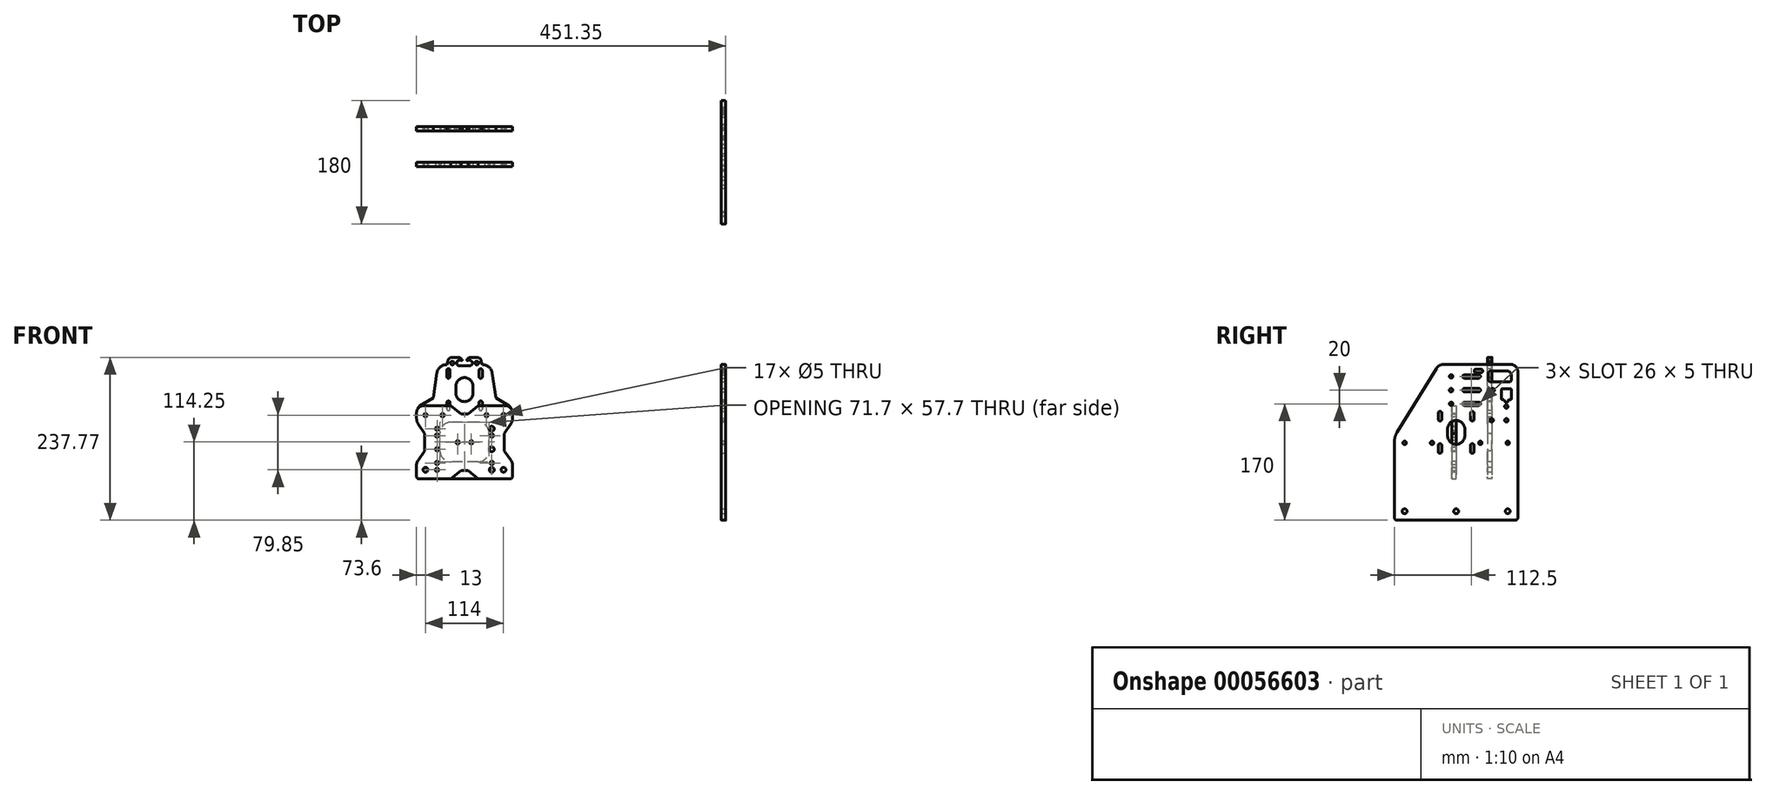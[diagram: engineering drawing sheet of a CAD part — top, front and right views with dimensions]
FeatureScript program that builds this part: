
annotation { "Feature Type Name" : "Feature", "Feature Type Description" : "" }
export const myFeature = defineFeature(function(context is Context, id is Id, definition is map)
    precondition{}
    {
        {
            var Q0;
            Q0=qCreatedBy(makeId("Right.planeOp"),FACE);
            var sketch = newSketch(context, id + "F0", { "sketchPlane" : qUnion([Q0])});
            skLineSegment(sketch, "E0", {"start": v(-28.77, 108.05) * mm, "end": v(-86.28, 14.78) * mm});
            skLineSegment(sketch, "E1", {"start": v(-90, 1.66) * mm, "end": v(-90, -110.25) * mm});
            skLineSegment(sketch, "E2", {"start": v(-86.5, -113.75) * mm, "end": v(86.5, -113.75) * mm});
            skLineSegment(sketch, "E3", {"start": v(90, -110.25) * mm, "end": v(90, 103.75) * mm});
            skLineSegment(sketch, "E4", {"start": v(80, 113.75) * mm, "end": v(-18.55, 113.75) * mm});
            skLineSegment(sketch, "E5", {"start": v(0, -113.75) * mm, "end": v(0, 0) * mm, "construction": true});
            skLineSegment(sketch, "E6", {"start": v(0, 0) * mm, "end": v(0, 113.75) * mm, "construction": true});
            skPoint(sketch, "E7.visualSharp", {"position": v(-25.25, 113.75) * mm});
            skArc(sketch, "E7.filletArc", {"start": v(-18.55, 113.75) * mm, "mid": v(-24.4, 112.23) * mm, "end": v(-28.77, 108.05) * mm});
            skPoint(sketch, "E8.visualSharp", {"position": v(90, 113.75) * mm});
            skArc(sketch, "E8.filletArc", {"start": v(90, 103.75) * mm, "mid": v(87.07, 110.82) * mm, "end": v(80, 113.75) * mm});
            skPoint(sketch, "E9.visualSharp", {"position": v(-90, -113.75) * mm});
            skArc(sketch, "E9.filletArc", {"start": v(-90, -110.25) * mm, "mid": v(-88.97, -112.72) * mm, "end": v(-86.5, -113.75) * mm});
            skPoint(sketch, "E10.visualSharp", {"position": v(90, -113.75) * mm});
            skArc(sketch, "E10.filletArc", {"start": v(86.5, -113.75) * mm, "mid": v(88.97, -112.72) * mm, "end": v(90, -110.25) * mm});
            skPoint(sketch, "E11.visualSharp", {"position": v(-90, 8.75) * mm});
            skArc(sketch, "E11.filletArc", {"start": v(-86.28, 14.78) * mm, "mid": v(-89.05, 8.48) * mm, "end": v(-90, 1.66) * mm});
            skSolve(sketch);
        }
        {
            var Q0;
            Q0 = qSketchRegion(id + "F0", true);
            extrude(context, id + "F1", {"entities" : qUnion([Q0]), "depth" : 6.35 * mm});
        }
        {
            var Q0;
            Q0=makeQuery(id+"F1.opExtrude","CAP_FACE",FACE,{"disambiguationData":[OSD([sQuery(id+"F0.wireOp",EDGE,"E0"),sQuery(id+"F0.wireOp",EDGE,"E1"),sQuery(id+"F0.wireOp",EDGE,"E2"),sQuery(id+"F0.wireOp",EDGE,"E3"),sQuery(id+"F0.wireOp",EDGE,"E4"),sQuery(id+"F0.wireOp",EDGE,"E7.filletArc"),sQuery(id+"F0.wireOp",EDGE,"E8.filletArc"),sQuery(id+"F0.wireOp",EDGE,"E9.filletArc"),sQuery(id+"F0.wireOp",EDGE,"E10.filletArc"),sQuery(id+"F0.wireOp",EDGE,"E11.filletArc")])],"isStart":false});
            var sketch = newSketch(context, id + "F2", { "sketchPlane" : qUnion([Q0])});
            skLineSegment(sketch, "E12", {"start": v(0, 0) * mm, "end": v(0, -100.75) * mm, "construction": true});
            skLineSegment(sketch, "E13", {"start": v(0, -100.75) * mm, "end": v(75.3, -100.75) * mm, "construction": true});
            skLineSegment(sketch, "E14", {"start": v(0, -100.75) * mm, "end": v(-75.3, -100.75) * mm, "construction": true});
            skCircle(sketch, "E15", {"center": v(-75.3, -100.75) * mm, "radius": 3.57 * mm});
            skCircle(sketch, "E16", {"center": v(75.3, -100.75) * mm, "radius": 3.57 * mm});
            skCircle(sketch, "E17", {"center": v(0, -100.75) * mm, "radius": 3.57 * mm});
            skLineSegment(sketch, "E18", {"start": v(-75.3, -0.75) * mm, "end": v(-35.3, -0.75) * mm, "construction": true});
            skLineSegment(sketch, "E19", {"start": v(-35.3, -0.75) * mm, "end": v(0, -0.75) * mm, "construction": true});
            skLineSegment(sketch, "E20", {"start": v(0, -0.75) * mm, "end": v(35.3, -0.75) * mm, "construction": true});
            skLineSegment(sketch, "E21", {"start": v(35.3, -0.75) * mm, "end": v(75.3, -0.75) * mm, "construction": true});
            skCircle(sketch, "E22", {"center": v(-75.3, -0.75) * mm, "radius": 2.5 * mm});
            skCircle(sketch, "E23", {"center": v(-35.3, -0.75) * mm, "radius": 2.5 * mm});
            skCircle(sketch, "E24", {"center": v(35.3, -0.75) * mm, "radius": 2.5 * mm});
            skCircle(sketch, "E25", {"center": v(75.3, -0.75) * mm, "radius": 2.5 * mm});
            skLineSegment(sketch, "E26", {"start": v(-75.3, -0.75) * mm, "end": v(-75.3, -100.75) * mm, "construction": true});
            skLineSegment(sketch, "E27", {"start": v(75.3, -0.75) * mm, "end": v(75.3, -100.75) * mm, "construction": true});
            skSolve(sketch);
        }
        {
            var Q0;
            Q0 = qSketchRegion(id + "F2", true);
            extrude(context, id + "F3", {"entities" : qUnion([Q0]), "operationType" : NewBodyOperationType.REMOVE, "endBound" : BoundingType.THROUGH_ALL, "oppositeDirection" : true, "depth" : 25 * mm});
        }
        {
            var Q0;
            Q0=makeQuery(id+"F1.opExtrude","CAP_FACE",FACE,{"disambiguationData":[OSD([sQuery(id+"F0.wireOp",EDGE,"E0"),sQuery(id+"F0.wireOp",EDGE,"E1"),sQuery(id+"F0.wireOp",EDGE,"E2"),sQuery(id+"F0.wireOp",EDGE,"E3"),sQuery(id+"F0.wireOp",EDGE,"E4"),sQuery(id+"F0.wireOp",EDGE,"E7.filletArc"),sQuery(id+"F0.wireOp",EDGE,"E8.filletArc"),sQuery(id+"F0.wireOp",EDGE,"E9.filletArc"),sQuery(id+"F0.wireOp",EDGE,"E10.filletArc"),sQuery(id+"F0.wireOp",EDGE,"E11.filletArc")])],"isStart":false});
            var sketch = newSketch(context, id + "F4", { "sketchPlane" : qUnion([Q0])});
            skArc(sketch, "E28", {"start": v(-12.5, 9.55) * mm, "mid": v(0, -2.95) * mm, "end": v(12.5, 9.55) * mm});
            skLineSegment(sketch, "E29", {"start": v(-12.5, 9.55) * mm, "end": v(-12.5, 19.55) * mm});
            skLineSegment(sketch, "E30", {"start": v(12.5, 19.55) * mm, "end": v(12.5, 9.55) * mm});
            skArc(sketch, "E31", {"start": v(-12.5, 19.55) * mm, "mid": v(0, 32.05) * mm, "end": v(12.5, 19.55) * mm});
            skLineSegment(sketch, "E32", {"start": v(0, 19.55) * mm, "end": v(0, 9.55) * mm, "construction": true});
            skLineSegment(sketch, "E33", {"start": v(-35.3, -0.75) * mm, "end": v(35.3, -0.75) * mm, "construction": true});
            skLineSegment(sketch, "E34", {"start": v(-23.57, 42.62) * mm, "end": v(-23.57, 33.62) * mm, "construction": true});
            skArc(sketch, "E35", {"start": v(-21.02, 42.62) * mm, "mid": v(-23.57, 45.17) * mm, "end": v(-26.12, 42.62) * mm});
            skArc(sketch, "E36", {"start": v(-26.12, 33.62) * mm, "mid": v(-23.57, 31.07) * mm, "end": v(-21.02, 33.62) * mm});
            skLineSegment(sketch, "E37", {"start": v(-21.02, 42.62) * mm, "end": v(-21.02, 33.62) * mm});
            skLineSegment(sketch, "E38", {"start": v(-26.12, 33.62) * mm, "end": v(-26.12, 42.62) * mm});
            skLineSegment(sketch, "E39", {"start": v(-12.5, 14.55) * mm, "end": v(12.5, 14.55) * mm, "construction": true});
            skLineSegment(sketch, "E40.MirrorCS", {"start": v(23.57, 42.62) * mm, "end": v(23.57, 33.62) * mm, "construction": true});
            skArc(sketch, "E41.MirrorCS", {"start": v(26.12, 33.62) * mm, "mid": v(23.57, 31.07) * mm, "end": v(21.02, 33.62) * mm});
            skLineSegment(sketch, "E42.MirrorCS", {"start": v(21.02, 42.62) * mm, "end": v(21.02, 33.62) * mm});
            skArc(sketch, "E43.MirrorCS", {"start": v(21.02, 42.62) * mm, "mid": v(23.57, 45.17) * mm, "end": v(26.12, 42.62) * mm});
            skLineSegment(sketch, "E44.MirrorCS", {"start": v(26.12, 33.62) * mm, "end": v(26.12, 42.62) * mm});
            skArc(sketch, "E45.MirrorCS", {"start": v(26.12, -4.52) * mm, "mid": v(23.57, -1.97) * mm, "end": v(21.02, -4.52) * mm});
            skLineSegment(sketch, "E46.MirrorCS", {"start": v(26.12, -4.52) * mm, "end": v(26.12, -13.52) * mm});
            skLineSegment(sketch, "E47.MirrorCS", {"start": v(-23.57, -13.52) * mm, "end": v(-23.57, -4.52) * mm, "construction": true});
            skLineSegment(sketch, "E48.MirrorCS", {"start": v(23.57, -13.52) * mm, "end": v(23.57, -4.52) * mm, "construction": true});
            skArc(sketch, "E49.MirrorCS", {"start": v(21.02, -13.52) * mm, "mid": v(23.57, -16.07) * mm, "end": v(26.12, -13.52) * mm});
            skLineSegment(sketch, "E50.MirrorCS", {"start": v(21.02, -13.52) * mm, "end": v(21.02, -4.52) * mm});
            skArc(sketch, "E51.MirrorCS", {"start": v(-26.12, -4.52) * mm, "mid": v(-23.57, -1.97) * mm, "end": v(-21.02, -4.52) * mm});
            skLineSegment(sketch, "E52.MirrorCS", {"start": v(-21.02, -13.52) * mm, "end": v(-21.02, -4.52) * mm});
            skArc(sketch, "E53.MirrorCS", {"start": v(-21.02, -13.52) * mm, "mid": v(-23.57, -16.07) * mm, "end": v(-26.12, -13.52) * mm});
            skLineSegment(sketch, "E54.MirrorCS", {"start": v(-26.12, -4.52) * mm, "end": v(-26.12, -13.52) * mm});
            skLineSegment(sketch, "E55", {"start": v(-23.57, 38.12) * mm, "end": v(23.57, -9.02) * mm, "construction": true});
            skLineSegment(sketch, "E56", {"start": v(23.57, -9.02) * mm, "end": v(-23.57, -9.02) * mm, "construction": true});
            skLineSegment(sketch, "E57", {"start": v(-23.57, -9.02) * mm, "end": v(23.57, 38.12) * mm, "construction": true});
            skSolve(sketch);
        }
        {
            var Q0;
            Q0 = qSketchRegion(id + "F4", true);
            extrude(context, id + "F5", {"entities" : qUnion([Q0]), "operationType" : NewBodyOperationType.REMOVE, "endBound" : BoundingType.THROUGH_ALL, "oppositeDirection" : true, "depth" : 25 * mm});
        }
        {
            var Q0;
            Q0=makeQuery(id+"F1.opExtrude","CAP_FACE",FACE,{"disambiguationData":[OSD([sQuery(id+"F0.wireOp",EDGE,"E0"),sQuery(id+"F0.wireOp",EDGE,"E1"),sQuery(id+"F0.wireOp",EDGE,"E2"),sQuery(id+"F0.wireOp",EDGE,"E3"),sQuery(id+"F0.wireOp",EDGE,"E4"),sQuery(id+"F0.wireOp",EDGE,"E7.filletArc"),sQuery(id+"F0.wireOp",EDGE,"E8.filletArc"),sQuery(id+"F0.wireOp",EDGE,"E9.filletArc"),sQuery(id+"F0.wireOp",EDGE,"E10.filletArc"),sQuery(id+"F0.wireOp",EDGE,"E11.filletArc")])],"isStart":false});
            var sketch = newSketch(context, id + "F6", { "sketchPlane" : qUnion([Q0])});
            skCircle(sketch, "E58", {"center": v(-7.35, 96.25) * mm, "radius": 2.5 * mm});
            skLineSegment(sketch, "E59", {"start": v(-7.35, 96.25) * mm, "end": v(12, 96.25) * mm, "construction": true});
            skLineSegment(sketch, "E60", {"start": v(12, 96.25) * mm, "end": v(33, 96.25) * mm, "construction": true});
            skArc(sketch, "E61", {"start": v(12, 93.75) * mm, "mid": v(9.5, 96.25) * mm, "end": v(12, 98.75) * mm});
            skArc(sketch, "E62", {"start": v(33, 98.75) * mm, "mid": v(35.5, 96.25) * mm, "end": v(33, 93.75) * mm});
            skLineSegment(sketch, "E63", {"start": v(12, 98.75) * mm, "end": v(33, 98.75) * mm});
            skLineSegment(sketch, "E64", {"start": v(12, 93.75) * mm, "end": v(33, 93.75) * mm});
            skCircle(sketch, "E65.0.1.0", {"center": v(-7.35, 76.25) * mm, "radius": 2.5 * mm});
            skLineSegment(sketch, "E65.0.1.1", {"start": v(-7.35, 76.25) * mm, "end": v(12, 76.25) * mm, "construction": true});
            skArc(sketch, "E65.0.1.2", {"start": v(12, 73.75) * mm, "mid": v(9.5, 76.25) * mm, "end": v(12, 78.75) * mm});
            skLineSegment(sketch, "E65.0.1.3", {"start": v(12, 78.75) * mm, "end": v(33, 78.75) * mm});
            skLineSegment(sketch, "E65.0.1.4", {"start": v(12, 73.75) * mm, "end": v(33, 73.75) * mm});
            skArc(sketch, "E65.0.1.5", {"start": v(33, 78.75) * mm, "mid": v(35.5, 76.25) * mm, "end": v(33, 73.75) * mm});
            skCircle(sketch, "E65.0.2.0", {"center": v(-7.35, 56.25) * mm, "radius": 2.5 * mm});
            skLineSegment(sketch, "E65.0.2.1", {"start": v(-7.35, 56.25) * mm, "end": v(12, 56.25) * mm, "construction": true});
            skArc(sketch, "E65.0.2.2", {"start": v(12, 53.75) * mm, "mid": v(9.5, 56.25) * mm, "end": v(12, 58.75) * mm});
            skLineSegment(sketch, "E65.0.2.3", {"start": v(12, 58.75) * mm, "end": v(33, 58.75) * mm});
            skLineSegment(sketch, "E65.0.2.4", {"start": v(12, 53.75) * mm, "end": v(33, 53.75) * mm});
            skArc(sketch, "E65.0.2.5", {"start": v(33, 58.75) * mm, "mid": v(35.5, 56.25) * mm, "end": v(33, 53.75) * mm});
            skLineSegment(sketch, "E65.direction1", {"start": v(-7.35, 96.25) * mm, "end": v(-7.35, 96.25) * mm});
            skLineSegment(sketch, "E65.direction2", {"start": v(-7.35, 96.25) * mm, "end": v(-7.35, 76.25) * mm, "construction": true});
            skLineSegment(sketch, "E66", {"start": v(33, 76.25) * mm, "end": v(12, 76.25) * mm, "construction": true});
            skLineSegment(sketch, "E67", {"start": v(12, 56.25) * mm, "end": v(33, 56.25) * mm, "construction": true});
            skLineSegment(sketch, "E68", {"start": v(33, 76.25) * mm, "end": v(53.35, 76.25) * mm, "construction": true});
            skPoint(sketch, "E68.endSnap0", {"position": v(35.5, 76.25) * mm});
            skCircle(sketch, "E69", {"center": v(53.35, 76.25) * mm, "radius": 2.5 * mm});
            skSolve(sketch);
        }
        {
            var Q0;
            Q0 = qSketchRegion(id + "F6", true);
            extrude(context, id + "F7", {"entities" : qUnion([Q0]), "operationType" : NewBodyOperationType.REMOVE, "endBound" : BoundingType.THROUGH_ALL, "oppositeDirection" : true, "depth" : 25 * mm});
        }
        {
            var Q0;
            Q0=makeQuery(id+"F1.opExtrude","CAP_FACE",FACE,{"disambiguationData":[OSD([sQuery(id+"F0.wireOp",EDGE,"E0"),sQuery(id+"F0.wireOp",EDGE,"E1"),sQuery(id+"F0.wireOp",EDGE,"E2"),sQuery(id+"F0.wireOp",EDGE,"E3"),sQuery(id+"F0.wireOp",EDGE,"E4"),sQuery(id+"F0.wireOp",EDGE,"E7.filletArc"),sQuery(id+"F0.wireOp",EDGE,"E8.filletArc"),sQuery(id+"F0.wireOp",EDGE,"E9.filletArc"),sQuery(id+"F0.wireOp",EDGE,"E10.filletArc"),sQuery(id+"F0.wireOp",EDGE,"E11.filletArc")])],"isStart":false});
            var sketch = newSketch(context, id + "F8", { "sketchPlane" : qUnion([Q0])});
            skLineSegment(sketch, "E70", {"start": v(12, 96.25) * mm, "end": v(33, 96.25) * mm, "construction": true});
            skLineSegment(sketch, "E71.bottom", {"start": v(28.1, 106.75) * mm, "end": v(36.9, 106.75) * mm});
            skLineSegment(sketch, "E71.top", {"start": v(28.1, 101.75) * mm, "end": v(36.9, 101.75) * mm});
            skLineSegment(sketch, "E71.left", {"start": v(26.5, 105.15) * mm, "end": v(26.5, 103.35) * mm});
            skLineSegment(sketch, "E71.right", {"start": v(38.5, 105.15) * mm, "end": v(38.5, 103.35) * mm});
            skPoint(sketch, "E72.visualSharp", {"position": v(26.5, 101.75) * mm});
            skArc(sketch, "E72.filletArc", {"start": v(26.5, 103.35) * mm, "mid": v(26.97, 102.22) * mm, "end": v(28.1, 101.75) * mm});
            skPoint(sketch, "E73.visualSharp", {"position": v(26.5, 106.75) * mm});
            skArc(sketch, "E73.filletArc", {"start": v(28.1, 106.75) * mm, "mid": v(26.97, 106.28) * mm, "end": v(26.5, 105.15) * mm});
            skPoint(sketch, "E74.visualSharp", {"position": v(38.5, 106.75) * mm});
            skArc(sketch, "E74.filletArc", {"start": v(38.5, 105.15) * mm, "mid": v(38.03, 106.28) * mm, "end": v(36.9, 106.75) * mm});
            skPoint(sketch, "E75.visualSharp", {"position": v(38.5, 101.75) * mm});
            skArc(sketch, "E75.filletArc", {"start": v(36.9, 101.75) * mm, "mid": v(38.03, 102.22) * mm, "end": v(38.5, 103.35) * mm});
            skLineSegment(sketch, "E76", {"start": v(26.5, 104.25) * mm, "end": v(38.5, 104.25) * mm, "construction": true});
            skLineSegment(sketch, "E77", {"start": v(32.5, 106.75) * mm, "end": v(32.5, 101.75) * mm, "construction": true});
            skLineSegment(sketch, "E78", {"start": v(22.5, 96.25) * mm, "end": v(22.5, 56.25) * mm, "construction": true});
            skPoint(sketch, "E78.endSnap0", {"position": v(22.5, 58.75) * mm});
            skLineSegment(sketch, "E79", {"start": v(12, 56.25) * mm, "end": v(33, 56.25) * mm, "construction": true});
            skSolve(sketch);
        }
        {
            var Q0;
            Q0 = qSketchRegion(id + "F8", true);
            extrude(context, id + "F9", {"entities" : qUnion([Q0]), "operationType" : NewBodyOperationType.REMOVE, "endBound" : BoundingType.THROUGH_ALL, "oppositeDirection" : true, "depth" : 25 * mm});
        }
        {
            var Q0;
            Q0=makeQuery(id+"F1.opExtrude","CAP_FACE",FACE,{"disambiguationData":[OSD([sQuery(id+"F0.wireOp",EDGE,"E0"),sQuery(id+"F0.wireOp",EDGE,"E1"),sQuery(id+"F0.wireOp",EDGE,"E2"),sQuery(id+"F0.wireOp",EDGE,"E3"),sQuery(id+"F0.wireOp",EDGE,"E4"),sQuery(id+"F0.wireOp",EDGE,"E7.filletArc"),sQuery(id+"F0.wireOp",EDGE,"E8.filletArc"),sQuery(id+"F0.wireOp",EDGE,"E9.filletArc"),sQuery(id+"F0.wireOp",EDGE,"E10.filletArc"),sQuery(id+"F0.wireOp",EDGE,"E11.filletArc")])],"isStart":false});
            var sketch = newSketch(context, id + "F10", { "sketchPlane" : qUnion([Q0])});
            skCircle(sketch, "E80", {"center": v(73.3, 52.25) * mm, "radius": 2.5 * mm});
            skLineSegment(sketch, "E81", {"start": v(73.3, 52.25) * mm, "end": v(73.3, 32.25) * mm, "construction": true});
            skCircle(sketch, "E82", {"center": v(73.3, 32.25) * mm, "radius": 2.5 * mm});
            skLineSegment(sketch, "E83", {"start": v(73.3, 32.25) * mm, "end": v(51.95, 32.25) * mm, "construction": true});
            skCircle(sketch, "E84", {"center": v(51.95, 32.25) * mm, "radius": 2.5 * mm});
            skLineSegment(sketch, "E85", {"start": v(12, 56.25) * mm, "end": v(33, 56.25) * mm, "construction": true});
            skLineSegment(sketch, "E86", {"start": v(33, 56.25) * mm, "end": v(33, 52.25) * mm, "construction": true});
            skLineSegment(sketch, "E87", {"start": v(33, 52.25) * mm, "end": v(73.3, 52.25) * mm, "construction": true});
            skSolve(sketch);
        }
        {
            var Q0;
            Q0 = qSketchRegion(id + "F10", true);
            extrude(context, id + "F11", {"entities" : qUnion([Q0]), "operationType" : NewBodyOperationType.REMOVE, "endBound" : BoundingType.THROUGH_ALL, "oppositeDirection" : true, "depth" : 25 * mm});
        }
        {
            var Q0;
            Q0=makeQuery(id+"F1.opExtrude","CAP_FACE",FACE,{"disambiguationData":[OSD([sQuery(id+"F0.wireOp",EDGE,"E0"),sQuery(id+"F0.wireOp",EDGE,"E1"),sQuery(id+"F0.wireOp",EDGE,"E2"),sQuery(id+"F0.wireOp",EDGE,"E3"),sQuery(id+"F0.wireOp",EDGE,"E4"),sQuery(id+"F0.wireOp",EDGE,"E7.filletArc"),sQuery(id+"F0.wireOp",EDGE,"E8.filletArc"),sQuery(id+"F0.wireOp",EDGE,"E9.filletArc"),sQuery(id+"F0.wireOp",EDGE,"E10.filletArc"),sQuery(id+"F0.wireOp",EDGE,"E11.filletArc")])],"isStart":false});
            var sketch = newSketch(context, id + "F12", { "sketchPlane" : qUnion([Q0])});
            skLineSegment(sketch, "E88", {"start": v(65.95, 76.8) * mm, "end": v(65.95, 63.85) * mm});
            skLineSegment(sketch, "E89", {"start": v(67.55, 62.25) * mm, "end": v(69.65, 62.25) * mm});
            skLineSegment(sketch, "E90", {"start": v(69.65, 62.25) * mm, "end": v(70.8, 60.75) * mm});
            skLineSegment(sketch, "E91", {"start": v(75.8, 60.75) * mm, "end": v(76.95, 62.25) * mm});
            skLineSegment(sketch, "E92", {"start": v(76.95, 62.25) * mm, "end": v(79.05, 62.25) * mm});
            skLineSegment(sketch, "E93", {"start": v(80.65, 63.85) * mm, "end": v(80.65, 76.8) * mm});
            skLineSegment(sketch, "E94", {"start": v(79.05, 78.4) * mm, "end": v(67.55, 78.4) * mm});
            skArc(sketch, "E95", {"start": v(70.8, 60.75) * mm, "mid": v(73.3, 58.25) * mm, "end": v(75.8, 60.75) * mm});
            skLineSegment(sketch, "E96", {"start": v(73.3, 60.75) * mm, "end": v(73.3, 52.25) * mm, "construction": true});
            skLineSegment(sketch, "E97", {"start": v(73.3, 78.4) * mm, "end": v(73.3, 60.75) * mm, "construction": true});
            skLineSegment(sketch, "E98", {"start": v(65.95, 70.32) * mm, "end": v(80.65, 70.32) * mm, "construction": true});
            skPoint(sketch, "E99.visualSharp", {"position": v(65.95, 62.25) * mm});
            skArc(sketch, "E99.filletArc", {"start": v(65.95, 63.85) * mm, "mid": v(66.42, 62.72) * mm, "end": v(67.55, 62.25) * mm});
            skPoint(sketch, "E100.visualSharp", {"position": v(65.95, 78.4) * mm});
            skArc(sketch, "E100.filletArc", {"start": v(67.55, 78.4) * mm, "mid": v(66.42, 77.93) * mm, "end": v(65.95, 76.8) * mm});
            skPoint(sketch, "E101.visualSharp", {"position": v(80.65, 78.4) * mm});
            skArc(sketch, "E101.filletArc", {"start": v(80.65, 76.8) * mm, "mid": v(80.18, 77.93) * mm, "end": v(79.05, 78.4) * mm});
            skPoint(sketch, "E102.visualSharp", {"position": v(80.65, 62.25) * mm});
            skArc(sketch, "E102.filletArc", {"start": v(79.05, 62.25) * mm, "mid": v(80.18, 62.72) * mm, "end": v(80.65, 63.85) * mm});
            skLineSegment(sketch, "E103", {"start": v(80.65, 91.4) * mm, "end": v(80.65, 97.6) * mm});
            skLineSegment(sketch, "E104", {"start": v(74, 104.25) * mm, "end": v(50.3, 104.25) * mm});
            skLineSegment(sketch, "E105", {"start": v(47.15, 101.1) * mm, "end": v(47.15, 91.4) * mm});
            skLineSegment(sketch, "E106", {"start": v(50.3, 88.25) * mm, "end": v(77.5, 88.25) * mm});
            skPoint(sketch, "E107.visualSharp", {"position": v(80.65, 104.25) * mm});
            skArc(sketch, "E107.filletArc", {"start": v(80.65, 97.6) * mm, "mid": v(78.7, 102.3) * mm, "end": v(74, 104.25) * mm});
            skPoint(sketch, "E108.visualSharp", {"position": v(80.65, 88.25) * mm});
            skArc(sketch, "E108.filletArc", {"start": v(77.5, 88.25) * mm, "mid": v(79.73, 89.17) * mm, "end": v(80.65, 91.4) * mm});
            skPoint(sketch, "E109.visualSharp", {"position": v(47.15, 88.25) * mm});
            skArc(sketch, "E109.filletArc", {"start": v(47.15, 91.4) * mm, "mid": v(48.07, 89.17) * mm, "end": v(50.3, 88.25) * mm});
            skPoint(sketch, "E110.visualSharp", {"position": v(47.15, 104.25) * mm});
            skArc(sketch, "E110.filletArc", {"start": v(50.3, 104.25) * mm, "mid": v(48.07, 103.33) * mm, "end": v(47.15, 101.1) * mm});
            skSolve(sketch);
        }
        {
            var Q0;
            Q0 = qSketchRegion(id + "F12", true);
            extrude(context, id + "F13", {"entities" : qUnion([Q0]), "operationType" : NewBodyOperationType.REMOVE, "endBound" : BoundingType.THROUGH_ALL, "oppositeDirection" : true, "depth" : 25 * mm});
        }
        {
            var Q0;
            Q0=makeQuery(id+"F1.opExtrude","SWEPT_BODY",BODY,{"disambiguationData":[OSD([sQuery(id+"F0.wireOp",EDGE,"E0"),sQuery(id+"F0.wireOp",EDGE,"E1"),sQuery(id+"F0.wireOp",EDGE,"E2"),sQuery(id+"F0.wireOp",EDGE,"E3"),sQuery(id+"F0.wireOp",EDGE,"E4"),sQuery(id+"F0.wireOp",EDGE,"E7.filletArc"),sQuery(id+"F0.wireOp",EDGE,"E8.filletArc"),sQuery(id+"F0.wireOp",EDGE,"E9.filletArc"),sQuery(id+"F0.wireOp",EDGE,"E10.filletArc"),sQuery(id+"F0.wireOp",EDGE,"E11.filletArc")])]});
            transform(context, id + "F14", {"entities" : qUnion([Q0]), "transformType" : TransformType.TRANSLATION_3D, "dx" : (750 / 2) * mm, "dy" : 0 * mm, "dz" : 0 * mm, "makeCopy" : false});
        }
        {
            var Q0;
            Q0=qCreatedBy(makeId("Front.planeOp"),FACE);
            var sketch = newSketch(context, id + "F15", { "sketchPlane" : qUnion([Q0])});
            skLineSegment(sketch, "E111", {"start": v(0, 0) * mm, "end": v(0, 41.2) * mm, "construction": true});
            skLineSegment(sketch, "E112", {"start": v(0, 0) * mm, "end": v(0, -41.2) * mm, "construction": true});
            skLineSegment(sketch, "E113", {"start": v(0, 41.2) * mm, "end": v(5, 41.2) * mm});
            skLineSegment(sketch, "E114", {"start": v(20, 53.35) * mm, "end": v(5, 41.2) * mm});
            skLineSegment(sketch, "E115", {"start": v(20, 53.35) * mm, "end": v(70, 53.35) * mm});
            skLineSegment(sketch, "E116", {"start": v(70, 53.35) * mm, "end": v(70, 30.5) * mm});
            skLineSegment(sketch, "E117", {"start": v(70, 30.5) * mm, "end": v(58, 12.75) * mm});
            skLineSegment(sketch, "E118", {"start": v(58, 12.75) * mm, "end": v(58, -12.75) * mm});
            skLineSegment(sketch, "E119", {"start": v(58, -12.75) * mm, "end": v(70, -29.25) * mm});
            skLineSegment(sketch, "E120", {"start": v(70, -29.25) * mm, "end": v(70, -53.35) * mm});
            skLineSegment(sketch, "E121", {"start": v(70, -53.35) * mm, "end": v(20, -53.35) * mm});
            skLineSegment(sketch, "E122", {"start": v(20, -53.35) * mm, "end": v(5, -41.2) * mm});
            skLineSegment(sketch, "E123", {"start": v(5, -41.2) * mm, "end": v(0, -41.2) * mm});
            skLineSegment(sketch, "E124", {"start": v(20, 53.35) * mm, "end": v(20, -53.35) * mm, "construction": true});
            skLineSegment(sketch, "E125", {"start": v(0, 41.2) * mm, "end": v(0, 53.35) * mm, "construction": true});
            skLineSegment(sketch, "E126", {"start": v(0, 53.35) * mm, "end": v(20, 53.35) * mm, "construction": true});
            skLineSegment(sketch, "E127", {"start": v(0, -41.2) * mm, "end": v(0, -53.35) * mm, "construction": true});
            skLineSegment(sketch, "E128", {"start": v(0, -53.35) * mm, "end": v(20, -53.35) * mm, "construction": true});
            skLineSegment(sketch, "E129", {"start": v(5, 41.2) * mm, "end": v(5, -41.2) * mm, "construction": true});
            skLineSegment(sketch, "E130", {"start": v(0, 0) * mm, "end": v(58, 0) * mm, "construction": true});
            skLineSegment(sketch, "E131", {"start": v(70, 30.5) * mm, "end": v(70, -29.25) * mm, "construction": true});
            skLineSegment(sketch, "E132.MirrorCS", {"start": v(-5, -41.2) * mm, "end": v(0, -41.2) * mm});
            skLineSegment(sketch, "E133.MirrorCS", {"start": v(-20, -53.35) * mm, "end": v(-5, -41.2) * mm});
            skLineSegment(sketch, "E134.MirrorCS", {"start": v(-70, -53.35) * mm, "end": v(-20, -53.35) * mm});
            skLineSegment(sketch, "E135.MirrorCS", {"start": v(-70, -29.25) * mm, "end": v(-70, -53.35) * mm});
            skLineSegment(sketch, "E136.MirrorCS", {"start": v(-58, -12.75) * mm, "end": v(-70, -29.25) * mm});
            skLineSegment(sketch, "E137.MirrorCS", {"start": v(-58, 12.75) * mm, "end": v(-58, -12.75) * mm});
            skLineSegment(sketch, "E138.MirrorCS", {"start": v(-70, 30.5) * mm, "end": v(-58, 12.75) * mm});
            skLineSegment(sketch, "E139.MirrorCS", {"start": v(-70, 53.35) * mm, "end": v(-70, 30.5) * mm});
            skLineSegment(sketch, "E140.MirrorCS", {"start": v(-20, 53.35) * mm, "end": v(-70, 53.35) * mm});
            skLineSegment(sketch, "E141.MirrorCS", {"start": v(0, 41.2) * mm, "end": v(-5, 41.2) * mm});
            skLineSegment(sketch, "E142.MirrorCS", {"start": v(-20, 53.35) * mm, "end": v(-5, 41.2) * mm});
            skSolve(sketch);
        }
        {
            var Q0;
            Q0 = qSketchRegion(id + "F15", true);
            extrude(context, id + "F16", {"entities" : qUnion([Q0]), "depth" : 6.35 * mm});
        }
        {
            var Q0;
            Q0=makeQuery(id+"F16.opExtrude","CAP_FACE",FACE,{"disambiguationData":[OSD([sQuery(id+"F15.wireOp",EDGE,"E113"),sQuery(id+"F15.wireOp",EDGE,"E114"),sQuery(id+"F15.wireOp",EDGE,"E115"),sQuery(id+"F15.wireOp",EDGE,"E116"),sQuery(id+"F15.wireOp",EDGE,"E117"),sQuery(id+"F15.wireOp",EDGE,"E118"),sQuery(id+"F15.wireOp",EDGE,"E119"),sQuery(id+"F15.wireOp",EDGE,"E120"),sQuery(id+"F15.wireOp",EDGE,"E121"),sQuery(id+"F15.wireOp",EDGE,"E122"),sQuery(id+"F15.wireOp",EDGE,"E123"),sQuery(id+"F15.wireOp",EDGE,"E132.MirrorCS"),sQuery(id+"F15.wireOp",EDGE,"E133.MirrorCS"),sQuery(id+"F15.wireOp",EDGE,"E134.MirrorCS"),sQuery(id+"F15.wireOp",EDGE,"E135.MirrorCS"),sQuery(id+"F15.wireOp",EDGE,"E136.MirrorCS"),sQuery(id+"F15.wireOp",EDGE,"E137.MirrorCS"),sQuery(id+"F15.wireOp",EDGE,"E138.MirrorCS"),sQuery(id+"F15.wireOp",EDGE,"E139.MirrorCS"),sQuery(id+"F15.wireOp",EDGE,"E140.MirrorCS"),sQuery(id+"F15.wireOp",EDGE,"E141.MirrorCS"),sQuery(id+"F15.wireOp",EDGE,"E142.MirrorCS")])],"isStart":false});
            var sketch = newSketch(context, id + "F17", { "sketchPlane" : qUnion([Q0])});
            skLineSegment(sketch, "E143", {"start": v(0, 0) * mm, "end": v(10, 0) * mm, "construction": true});
            skLineSegment(sketch, "E144", {"start": v(0, 0) * mm, "end": v(-10, 0) * mm, "construction": true});
            skCircle(sketch, "E145", {"center": v(-10, 0) * mm, "radius": 2.5 * mm});
            skCircle(sketch, "E146", {"center": v(10, 0) * mm, "radius": 2.5 * mm});
            skSolve(sketch);
        }
        {
            var Q0;
            Q0 = qSketchRegion(id + "F17", true);
            extrude(context, id + "F18", {"entities" : qUnion([Q0]), "operationType" : NewBodyOperationType.REMOVE, "endBound" : BoundingType.THROUGH_ALL, "oppositeDirection" : true, "depth" : 25 * mm});
        }
        {
            var Q0;
            Q0=makeQuery(id+"F16.opExtrude","CAP_FACE",FACE,{"disambiguationData":[OSD([sQuery(id+"F15.wireOp",EDGE,"E113"),sQuery(id+"F15.wireOp",EDGE,"E114"),sQuery(id+"F15.wireOp",EDGE,"E115"),sQuery(id+"F15.wireOp",EDGE,"E116"),sQuery(id+"F15.wireOp",EDGE,"E117"),sQuery(id+"F15.wireOp",EDGE,"E118"),sQuery(id+"F15.wireOp",EDGE,"E119"),sQuery(id+"F15.wireOp",EDGE,"E120"),sQuery(id+"F15.wireOp",EDGE,"E121"),sQuery(id+"F15.wireOp",EDGE,"E122"),sQuery(id+"F15.wireOp",EDGE,"E123"),sQuery(id+"F15.wireOp",EDGE,"E132.MirrorCS"),sQuery(id+"F15.wireOp",EDGE,"E133.MirrorCS"),sQuery(id+"F15.wireOp",EDGE,"E134.MirrorCS"),sQuery(id+"F15.wireOp",EDGE,"E135.MirrorCS"),sQuery(id+"F15.wireOp",EDGE,"E136.MirrorCS"),sQuery(id+"F15.wireOp",EDGE,"E137.MirrorCS"),sQuery(id+"F15.wireOp",EDGE,"E138.MirrorCS"),sQuery(id+"F15.wireOp",EDGE,"E139.MirrorCS"),sQuery(id+"F15.wireOp",EDGE,"E140.MirrorCS"),sQuery(id+"F15.wireOp",EDGE,"E141.MirrorCS"),sQuery(id+"F15.wireOp",EDGE,"E142.MirrorCS")])],"isStart":false});
            var sketch = newSketch(context, id + "F19", { "sketchPlane" : qUnion([Q0])});
            skLineSegment(sketch, "E147", {"start": v(0, 41.2) * mm, "end": v(0, -41.2) * mm, "construction": true});
            skLineSegment(sketch, "E148", {"start": v(32, 39.7) * mm, "end": v(57, 39.7) * mm, "construction": true});
            skCircle(sketch, "E149", {"center": v(32, 39.7) * mm, "radius": 2.5 * mm});
            skCircle(sketch, "E150", {"center": v(57, 39.7) * mm, "radius": 2.5 * mm});
            skCircle(sketch, "E151", {"center": v(57, -40.1) * mm, "radius": 3.57 * mm});
            skCircle(sketch, "E152.MirrorC", {"center": v(-57, -40.1) * mm, "radius": 3.57 * mm});
            skCircle(sketch, "E153.MirrorC", {"center": v(-57, 39.7) * mm, "radius": 2.5 * mm});
            skCircle(sketch, "E154.MirrorC", {"center": v(-32, 39.7) * mm, "radius": 2.5 * mm});
            skLineSegment(sketch, "E155", {"start": v(-57, 39.7) * mm, "end": v(-32, 39.7) * mm, "construction": true});
            skLineSegment(sketch, "E156", {"start": v(57, 39.7) * mm, "end": v(57, -40.1) * mm, "construction": true});
            skLineSegment(sketch, "E157", {"start": v(-57, 39.7) * mm, "end": v(-57, -40.1) * mm, "construction": true});
            skLineSegment(sketch, "E158", {"start": v(-57, -40.1) * mm, "end": v(57, -40.1) * mm, "construction": true});
            skLineSegment(sketch, "E159", {"start": v(-32, 39.7) * mm, "end": v(32, 39.7) * mm, "construction": true});
            skSolve(sketch);
        }
        {
            var Q0;
            Q0 = qSketchRegion(id + "F19", true);
            extrude(context, id + "F20", {"entities" : qUnion([Q0]), "operationType" : NewBodyOperationType.REMOVE, "endBound" : BoundingType.THROUGH_ALL, "oppositeDirection" : true, "depth" : 25 * mm});
        }
        {
            var Q0;
            Q0=makeQuery(id+"F16.opExtrude","CAP_FACE",FACE,{"disambiguationData":[OSD([sQuery(id+"F15.wireOp",EDGE,"E113"),sQuery(id+"F15.wireOp",EDGE,"E114"),sQuery(id+"F15.wireOp",EDGE,"E115"),sQuery(id+"F15.wireOp",EDGE,"E116"),sQuery(id+"F15.wireOp",EDGE,"E117"),sQuery(id+"F15.wireOp",EDGE,"E118"),sQuery(id+"F15.wireOp",EDGE,"E119"),sQuery(id+"F15.wireOp",EDGE,"E120"),sQuery(id+"F15.wireOp",EDGE,"E121"),sQuery(id+"F15.wireOp",EDGE,"E122"),sQuery(id+"F15.wireOp",EDGE,"E123"),sQuery(id+"F15.wireOp",EDGE,"E132.MirrorCS"),sQuery(id+"F15.wireOp",EDGE,"E133.MirrorCS"),sQuery(id+"F15.wireOp",EDGE,"E134.MirrorCS"),sQuery(id+"F15.wireOp",EDGE,"E135.MirrorCS"),sQuery(id+"F15.wireOp",EDGE,"E136.MirrorCS"),sQuery(id+"F15.wireOp",EDGE,"E137.MirrorCS"),sQuery(id+"F15.wireOp",EDGE,"E138.MirrorCS"),sQuery(id+"F15.wireOp",EDGE,"E139.MirrorCS"),sQuery(id+"F15.wireOp",EDGE,"E140.MirrorCS"),sQuery(id+"F15.wireOp",EDGE,"E141.MirrorCS"),sQuery(id+"F15.wireOp",EDGE,"E142.MirrorCS")])],"isStart":false});
            var sketch = newSketch(context, id + "F21", { "sketchPlane" : qUnion([Q0])});
            skLineSegment(sketch, "E160", {"start": v(0, 41.2) * mm, "end": v(0, -41.2) * mm, "construction": true});
            skLineSegment(sketch, "E161", {"start": v(39.8, 9.85) * mm, "end": v(39.8, -10.15) * mm, "construction": true});
            skLineSegment(sketch, "E162", {"start": v(39.8, -10.15) * mm, "end": v(39.8, -30.15) * mm, "construction": true});
            skLineSegment(sketch, "E163", {"start": v(39.8, 9.85) * mm, "end": v(39.8, 19.85) * mm, "construction": true});
            skLineSegment(sketch, "E164", {"start": v(39.8, -30.15) * mm, "end": v(39.8, -40.15) * mm, "construction": true});
            skCircle(sketch, "E165", {"center": v(39.8, 19.85) * mm, "radius": 3.57 * mm});
            skCircle(sketch, "E166", {"center": v(39.8, -10.15) * mm, "radius": 3.57 * mm});
            skCircle(sketch, "E167", {"center": v(39.8, -40.15) * mm, "radius": 3.57 * mm});
            skCircle(sketch, "E168", {"center": v(39.8, 9.85) * mm, "radius": 2.5 * mm});
            skCircle(sketch, "E169", {"center": v(39.8, -30.15) * mm, "radius": 2.5 * mm});
            skLineSegment(sketch, "E170", {"start": v(39.8, -10.15) * mm, "end": v(0, -10.15) * mm, "construction": true});
            skLineSegment(sketch, "E171", {"start": v(-40, 9.85) * mm, "end": v(-40, 19.85) * mm, "construction": true});
            skLineSegment(sketch, "E172", {"start": v(-40, -30.15) * mm, "end": v(-40, -40.15) * mm, "construction": true});
            skCircle(sketch, "E173", {"center": v(-40, 19.85) * mm, "radius": 2.5 * mm});
            skCircle(sketch, "E174", {"center": v(-40, 9.85) * mm, "radius": 2.5 * mm});
            skCircle(sketch, "E175", {"center": v(-40, -10.15) * mm, "radius": 2.5 * mm});
            skCircle(sketch, "E176", {"center": v(-40, -30.15) * mm, "radius": 2.5 * mm});
            skCircle(sketch, "E177", {"center": v(-40, -40.15) * mm, "radius": 2.5 * mm});
            skLineSegment(sketch, "E178", {"start": v(-40, -30.15) * mm, "end": v(-40, -10.15) * mm, "construction": true});
            skLineSegment(sketch, "E179", {"start": v(-40, 9.85) * mm, "end": v(-40, -10.15) * mm, "construction": true});
            skLineSegment(sketch, "E180", {"start": v(-40, -10.15) * mm, "end": v(0, -10.15) * mm, "construction": true});
            skSolve(sketch);
        }
        {
            var Q0;
            Q0 = qSketchRegion(id + "F21", true);
            extrude(context, id + "F22", {"entities" : qUnion([Q0]), "operationType" : NewBodyOperationType.REMOVE, "endBound" : BoundingType.THROUGH_ALL, "oppositeDirection" : true, "depth" : 25 * mm});
        }
        {
            var Q0;
            Q0=makeQuery(id+"F16.opExtrude","SWEPT_EDGE",EDGE,{"disambiguationData":[OSD([sQuery(id+"F15.wireOp",EDGE,"E139.MirrorCS"),sQuery(id+"F15.wireOp",EDGE,"E140.MirrorCS")])]});
            var Q1;
            Q1=makeQuery(id+"F16.opExtrude","SWEPT_EDGE",EDGE,{"disambiguationData":[OSD([sQuery(id+"F15.wireOp",EDGE,"E115"),sQuery(id+"F15.wireOp",EDGE,"E116")])]});
            fillet(context, id + "F23", {"entities" : qUnion([Q0, Q1]), "radius" : 9.6 * mm, "tangentPropagation" : true, "allowEdgeOverflow" : false});
        }
        {
            var Q0;
            Q0=makeQuery(id+"F16.opExtrude","SWEPT_EDGE",EDGE,{"disambiguationData":[OSD([sQuery(id+"F15.wireOp",EDGE,"E120"),sQuery(id+"F15.wireOp",EDGE,"E121")])]});
            var Q1;
            Q1=makeQuery(id+"F16.opExtrude","SWEPT_EDGE",EDGE,{"disambiguationData":[OSD([sQuery(id+"F15.wireOp",EDGE,"E134.MirrorCS"),sQuery(id+"F15.wireOp",EDGE,"E135.MirrorCS")])]});
            fillet(context, id + "F24", {"entities" : qUnion([Q0, Q1]), "radius" : 3.36 * mm, "tangentPropagation" : true, "allowEdgeOverflow" : false});
        }
        {
            var Q0;
            Q0=makeQuery(id+"F16.opExtrude","SWEPT_EDGE",EDGE,{"disambiguationData":[OSD([sQuery(id+"F15.wireOp",EDGE,"E116"),sQuery(id+"F15.wireOp",EDGE,"E117")])]});
            var Q1;
            Q1=makeQuery(id+"F16.opExtrude","SWEPT_EDGE",EDGE,{"disambiguationData":[OSD([sQuery(id+"F15.wireOp",EDGE,"E138.MirrorCS"),sQuery(id+"F15.wireOp",EDGE,"E139.MirrorCS")])]});
            fillet(context, id + "F25", {"entities" : qUnion([Q0, Q1]), "radius" : 14 * mm, "tangentPropagation" : true, "allowEdgeOverflow" : false});
        }
        {
            var Q0;
            Q0=makeQuery(id+"F16.opExtrude","SWEPT_EDGE",EDGE,{"disambiguationData":[OSD([sQuery(id+"F15.wireOp",EDGE,"E119"),sQuery(id+"F15.wireOp",EDGE,"E120")])]});
            var Q1;
            Q1=makeQuery(id+"F16.opExtrude","SWEPT_EDGE",EDGE,{"disambiguationData":[OSD([sQuery(id+"F15.wireOp",EDGE,"E135.MirrorCS"),sQuery(id+"F15.wireOp",EDGE,"E136.MirrorCS")])]});
            fillet(context, id + "F26", {"entities" : qUnion([Q0, Q1]), "radius" : 11 * mm, "tangentPropagation" : true, "allowEdgeOverflow" : false});
        }
        {
            var Q0;
            Q0=makeQuery(id+"F16.opExtrude","CAP_FACE",FACE,{"disambiguationData":[OSD([sQuery(id+"F15.wireOp",EDGE,"E113"),sQuery(id+"F15.wireOp",EDGE,"E114"),sQuery(id+"F15.wireOp",EDGE,"E115"),sQuery(id+"F15.wireOp",EDGE,"E116"),sQuery(id+"F15.wireOp",EDGE,"E117"),sQuery(id+"F15.wireOp",EDGE,"E118"),sQuery(id+"F15.wireOp",EDGE,"E119"),sQuery(id+"F15.wireOp",EDGE,"E120"),sQuery(id+"F15.wireOp",EDGE,"E121"),sQuery(id+"F15.wireOp",EDGE,"E122"),sQuery(id+"F15.wireOp",EDGE,"E123"),sQuery(id+"F15.wireOp",EDGE,"E132.MirrorCS"),sQuery(id+"F15.wireOp",EDGE,"E133.MirrorCS"),sQuery(id+"F15.wireOp",EDGE,"E134.MirrorCS"),sQuery(id+"F15.wireOp",EDGE,"E135.MirrorCS"),sQuery(id+"F15.wireOp",EDGE,"E136.MirrorCS"),sQuery(id+"F15.wireOp",EDGE,"E137.MirrorCS"),sQuery(id+"F15.wireOp",EDGE,"E138.MirrorCS"),sQuery(id+"F15.wireOp",EDGE,"E139.MirrorCS"),sQuery(id+"F15.wireOp",EDGE,"E140.MirrorCS"),sQuery(id+"F15.wireOp",EDGE,"E141.MirrorCS"),sQuery(id+"F15.wireOp",EDGE,"E142.MirrorCS")])],"isStart":true});
            cPlane(context, id + "F27", {"entities" : qUnion([Q0]), "cplaneType" : CPlaneType.OFFSET, "offset" : 46 * mm, "width" : 150 * mm, "height" : 150 * mm});
        }
        {
            var Q0;
            Q0=qCreatedBy(id+"F27.planeOp",FACE);
            var sketch = newSketch(context, id + "F28", { "sketchPlane" : qUnion([Q0])});
            skLineSegment(sketch, "E181", {"start": v(0, 0) * mm, "end": v(0, -53.35) * mm, "construction": true});
            skLineSegment(sketch, "E182", {"start": v(-67.5, 51.95) * mm, "end": v(-45.84, 64.81) * mm});
            skLineSegment(sketch, "E183", {"start": v(-45.84, 64.81) * mm, "end": v(-38.5, 113.35) * mm});
            skLineSegment(sketch, "E184", {"start": v(-38.5, 113.35) * mm, "end": v(-26, 113.35) * mm});
            skLineSegment(sketch, "E185", {"start": v(-26, 113.35) * mm, "end": v(-22.45, 124.02) * mm, "construction": true});
            skLineSegment(sketch, "E186", {"start": v(-22.45, 124.02) * mm, "end": v(0, 124.02) * mm, "construction": true});
            skLineSegment(sketch, "E187", {"start": v(0, 124.02) * mm, "end": v(0, 0) * mm, "construction": true});
            skLineSegment(sketch, "E188.MirrorCS", {"start": v(22.45, 124.02) * mm, "end": v(0, 124.02) * mm, "construction": true});
            skLineSegment(sketch, "E189.MirrorCS", {"start": v(26, 113.35) * mm, "end": v(22.45, 124.02) * mm, "construction": true});
            skLineSegment(sketch, "E190.MirrorCS", {"start": v(38.5, 113.35) * mm, "end": v(26, 113.35) * mm});
            skLineSegment(sketch, "E191.MirrorCS", {"start": v(45.84, 64.81) * mm, "end": v(38.5, 113.35) * mm});
            skLineSegment(sketch, "E192.MirrorCS", {"start": v(67.5, 51.95) * mm, "end": v(45.84, 64.81) * mm});
            skLineSegment(sketch, "E193", {"start": v(45.84, 64.81) * mm, "end": v(45.84, 113.35) * mm, "construction": true});
            skArc(sketch, "E194.0", {"start": v(70, 34.79) * mm, "mid": v(69.39, 30.69) * mm, "end": v(67.6, 26.95) * mm});
            skLineSegment(sketch, "E195.0", {"start": v(67.6, 26.95) * mm, "end": v(58, 12.75) * mm});
            skLineSegment(sketch, "E196.0", {"start": v(58, 12.75) * mm, "end": v(58, -12.75) * mm});
            skLineSegment(sketch, "E197.0", {"start": v(58, -12.75) * mm, "end": v(67.9, -26.36) * mm});
            skArc(sketch, "E198.0", {"start": v(67.9, -26.36) * mm, "mid": v(69.46, -29.43) * mm, "end": v(70, -32.83) * mm});
            skLineSegment(sketch, "E199.0", {"start": v(70, -32.83) * mm, "end": v(70, -49.99) * mm});
            skArc(sketch, "E200.0", {"start": v(70, -49.99) * mm, "mid": v(69.02, -52.37) * mm, "end": v(66.64, -53.35) * mm});
            skLineSegment(sketch, "E201.0", {"start": v(66.64, -53.35) * mm, "end": v(20, -53.35) * mm});
            skLineSegment(sketch, "E202.0", {"start": v(-66.64, -53.35) * mm, "end": v(-20, -53.35) * mm});
            skArc(sketch, "E203.0", {"start": v(-66.64, -53.35) * mm, "mid": v(-69.02, -52.37) * mm, "end": v(-70, -49.99) * mm});
            skLineSegment(sketch, "E204.0", {"start": v(-70, -32.83) * mm, "end": v(-70, -49.99) * mm});
            skArc(sketch, "E205.0", {"start": v(-70, -32.83) * mm, "mid": v(-69.46, -29.43) * mm, "end": v(-67.9, -26.36) * mm});
            skLineSegment(sketch, "E206.0", {"start": v(-58, -12.75) * mm, "end": v(-67.9, -26.36) * mm});
            skLineSegment(sketch, "E207.0", {"start": v(-58, 12.75) * mm, "end": v(-58, -12.75) * mm});
            skLineSegment(sketch, "E208.0", {"start": v(-67.6, 26.95) * mm, "end": v(-58, 12.75) * mm});
            skArc(sketch, "E209.0", {"start": v(-70, 34.79) * mm, "mid": v(-69.39, 30.69) * mm, "end": v(-67.6, 26.95) * mm});
            skLineSegment(sketch, "E210", {"start": v(70, 34.79) * mm, "end": v(67.5, 51.95) * mm});
            skLineSegment(sketch, "E211", {"start": v(-67.5, 51.95) * mm, "end": v(-70, 34.79) * mm});
            skLineSegment(sketch, "E212", {"start": v(20, -53.35) * mm, "end": v(-20, -53.35) * mm});
            skLineSegment(sketch, "E213", {"start": v(-67.5, 51.95) * mm, "end": v(-67.5, 104.82) * mm, "construction": true});
            skLineSegment(sketch, "E214", {"start": v(24.5, 117.85) * mm, "end": v(-24.5, 117.85) * mm, "construction": true});
            skLineSegment(sketch, "E215", {"start": v(26, 113.35) * mm, "end": v(24.5, 117.85) * mm});
            skLineSegment(sketch, "E216", {"start": v(-24.5, 117.85) * mm, "end": v(-26, 113.35) * mm});
            skArc(sketch, "E217", {"start": v(24.5, 117.85) * mm, "mid": v(22.7, 122.21) * mm, "end": v(18.33, 124.02) * mm});
            skArc(sketch, "E218.MirrorCS", {"start": v(-24.5, 117.85) * mm, "mid": v(-22.7, 122.21) * mm, "end": v(-18.33, 124.02) * mm});
            skLineSegment(sketch, "E219", {"start": v(18.33, 124.02) * mm, "end": v(-18.33, 124.02) * mm});
            skSolve(sketch);
        }
        {
            var Q0;
            Q0 = qSketchRegion(id + "F28", true);
            extrude(context, id + "F29", {"entities" : qUnion([Q0]), "depth" : 6.35 * mm});
        }
        {
            var Q0;
            Q0=makeQuery(id+"F29.opExtrude","CAP_FACE",FACE,{"disambiguationData":[OSD([sQuery(id+"F28.wireOp",EDGE,"Hsz0tEu8-2u2z-894v-u5uz-qeEPLO7T1y3h"),sQuery(id+"F28.wireOp",EDGE,"vEOOrqZs-7KoW-orxh-Vkwo-SEQycOVZhe9Y"),sQuery(id+"F28.wireOp",EDGE,"aVo1oUrC-5gOD-S3Gd-KdpA-WAxqIndI85XZ"),sQuery(id+"F28.wireOp",EDGE,"9HF069ls-R4vM-rCiR-Mglt-uF1vui31pR4p"),sQuery(id+"F28.wireOp",EDGE,"6UwIWVSN-CBoj-eV2b-T7fp-u49lRc933uwu"),sQuery(id+"F28.wireOp",EDGE,"xATdj4HU-5i3P-5F5E-4dWz-QLdLokjUGgyJ"),sQuery(id+"F28.wireOp",EDGE,"E182"),sQuery(id+"F28.wireOp",EDGE,"E183"),sQuery(id+"F28.wireOp",EDGE,"E184"),sQuery(id+"F28.wireOp",EDGE,"E185"),sQuery(id+"F28.wireOp",EDGE,"E186"),sQuery(id+"F28.wireOp",EDGE,"01ed5a7f-363f-42f9-805d-97d743e7f8c00.MirrorCS"),sQuery(id+"F28.wireOp",EDGE,"E188.MirrorCS"),sQuery(id+"F28.wireOp",EDGE,"E189.MirrorCS"),sQuery(id+"F28.wireOp",EDGE,"E190.MirrorCS"),sQuery(id+"F28.wireOp",EDGE,"E191.MirrorCS"),sQuery(id+"F28.wireOp",EDGE,"E192.MirrorCS"),sQuery(id+"F28.wireOp",EDGE,"01ed5a7f-363f-42f9-805d-97d743e7f8c06.MirrorCS"),sQuery(id+"F28.wireOp",EDGE,"01ed5a7f-363f-42f9-805d-97d743e7f8c08.MirrorCS"),sQuery(id+"F28.wireOp",EDGE,"01ed5a7f-363f-42f9-805d-97d743e7f8c09.MirrorCS"),sQuery(id+"F28.wireOp",EDGE,"orUJIb6K-YDtt-LamK-tEY8-xfgMmjDqjYYe"),sQuery(id+"F28.wireOp",EDGE,"c8cb6b1b-2073-4661-974d-9f2328fd6722"),sQuery(id+"F28.wireOp",EDGE,"7cc86124-f559-48ea-aabb-f436df0639fe0.MirrorCS"),sQuery(id+"F28.wireOp",EDGE,"7cc86124-f559-48ea-aabb-f436df0639fe1.MirrorCS")])],"isStart":true});
            var sketch = newSketch(context, id + "F30", { "sketchPlane" : qUnion([Q0])});
            skCircle(sketch, "E220.0", {"center": v(-57, 39.7) * mm, "radius": 2.5 * mm});
            skCircle(sketch, "E221.0", {"center": v(-32, 39.7) * mm, "radius": 2.5 * mm});
            skCircle(sketch, "E222.0", {"center": v(32, 39.7) * mm, "radius": 2.5 * mm});
            skCircle(sketch, "E223.0", {"center": v(57, 39.7) * mm, "radius": 2.5 * mm});
            skCircle(sketch, "E224.0", {"center": v(-57, -40.1) * mm, "radius": 3.57 * mm});
            skCircle(sketch, "E225.0", {"center": v(57, -40.1) * mm, "radius": 3.57 * mm});
            skSolve(sketch);
        }
        {
            var Q0;
            Q0 = qSketchRegion(id + "F30", true);
            extrude(context, id + "F31", {"entities" : qUnion([Q0]), "operationType" : NewBodyOperationType.REMOVE, "endBound" : BoundingType.THROUGH_ALL, "oppositeDirection" : true, "depth" : 25 * mm});
        }
        {
            var Q0;
            Q0=makeQuery(id+"F29.opExtrude","SWEPT_EDGE",EDGE,{"disambiguationData":[OSD([sQuery(id+"F28.wireOp",EDGE,"E183"),sQuery(id+"F28.wireOp",EDGE,"E184")])]});
            var Q1;
            Q1=makeQuery(id+"F29.opExtrude","SWEPT_EDGE",EDGE,{"disambiguationData":[OSD([sQuery(id+"F28.wireOp",EDGE,"E190.MirrorCS"),sQuery(id+"F28.wireOp",EDGE,"E191.MirrorCS")])]});
            fillet(context, id + "F32", {"entities" : qUnion([Q0, Q1]), "radius" : 13.7 * mm, "tangentPropagation" : true, "allowEdgeOverflow" : false});
        }
        {
            var Q0;
            Q0=makeQuery(id+"F29.opExtrude","SWEPT_EDGE",EDGE,{"disambiguationData":[OSD([sQuery(id+"F28.wireOp",EDGE,"E182"),sQuery(id+"F28.wireOp",EDGE,"E211")])]});
            var Q1;
            Q1=makeQuery(id+"F29.opExtrude","SWEPT_EDGE",EDGE,{"disambiguationData":[OSD([sQuery(id+"F28.wireOp",EDGE,"E192.MirrorCS"),sQuery(id+"F28.wireOp",EDGE,"E210")])]});
            fillet(context, id + "F33", {"entities" : qUnion([Q0, Q1]), "radius" : 5.5 * mm, "tangentPropagation" : true, "allowEdgeOverflow" : false});
        }
        {
            var Q0;
            Q0=makeQuery(id+"F29.opExtrude","CAP_FACE",FACE,{"disambiguationData":[OSD([sQuery(id+"F28.wireOp",EDGE,"E182"),sQuery(id+"F28.wireOp",EDGE,"E183"),sQuery(id+"F28.wireOp",EDGE,"E184"),sQuery(id+"F28.wireOp",EDGE,"E185"),sQuery(id+"F28.wireOp",EDGE,"E186"),sQuery(id+"F28.wireOp",EDGE,"E188.MirrorCS"),sQuery(id+"F28.wireOp",EDGE,"E189.MirrorCS"),sQuery(id+"F28.wireOp",EDGE,"E190.MirrorCS"),sQuery(id+"F28.wireOp",EDGE,"E191.MirrorCS"),sQuery(id+"F28.wireOp",EDGE,"E192.MirrorCS"),sQuery(id+"F28.wireOp",EDGE,"E194.0"),sQuery(id+"F28.wireOp",EDGE,"E195.0"),sQuery(id+"F28.wireOp",EDGE,"E196.0"),sQuery(id+"F28.wireOp",EDGE,"E197.0"),sQuery(id+"F28.wireOp",EDGE,"E198.0"),sQuery(id+"F28.wireOp",EDGE,"E199.0"),sQuery(id+"F28.wireOp",EDGE,"E200.0"),sQuery(id+"F28.wireOp",EDGE,"E201.0"),sQuery(id+"F28.wireOp",EDGE,"E202.0"),sQuery(id+"F28.wireOp",EDGE,"E203.0"),sQuery(id+"F28.wireOp",EDGE,"E204.0"),sQuery(id+"F28.wireOp",EDGE,"E205.0"),sQuery(id+"F28.wireOp",EDGE,"E206.0"),sQuery(id+"F28.wireOp",EDGE,"E207.0"),sQuery(id+"F28.wireOp",EDGE,"E208.0"),sQuery(id+"F28.wireOp",EDGE,"E209.0"),sQuery(id+"F28.wireOp",EDGE,"E210"),sQuery(id+"F28.wireOp",EDGE,"E211"),sQuery(id+"F28.wireOp",EDGE,"E212")])],"isStart":true});
            var sketch = newSketch(context, id + "F34", { "sketchPlane" : qUnion([Q0])});
            skLineSegment(sketch, "E226.bottom", {"start": v(-19.85, 29.35) * mm, "end": v(19.85, 29.35) * mm});
            skLineSegment(sketch, "E226.top", {"start": v(-19.85, -28.35) * mm, "end": v(19.85, -28.35) * mm});
            skLineSegment(sketch, "E226.left", {"start": v(-35.85, 13.35) * mm, "end": v(-35.85, -12.35) * mm});
            skLineSegment(sketch, "E226.right", {"start": v(35.85, 13.35) * mm, "end": v(35.85, -12.35) * mm});
            skLineSegment(sketch, "E227", {"start": v(0, 29.35) * mm, "end": v(0, 0) * mm, "construction": true});
            skLineSegment(sketch, "E228", {"start": v(0, 0) * mm, "end": v(0, -28.35) * mm, "construction": true});
            skPoint(sketch, "E229.visualSharp", {"position": v(-35.85, 29.35) * mm});
            skArc(sketch, "E229.filletArc", {"start": v(-19.85, 29.35) * mm, "mid": v(-31.16, 24.66) * mm, "end": v(-35.85, 13.35) * mm});
            skPoint(sketch, "E230.visualSharp", {"position": v(35.85, 29.35) * mm});
            skArc(sketch, "E230.filletArc", {"start": v(35.85, 13.35) * mm, "mid": v(31.16, 24.66) * mm, "end": v(19.85, 29.35) * mm});
            skPoint(sketch, "E231.visualSharp", {"position": v(35.85, -28.35) * mm});
            skArc(sketch, "E231.filletArc", {"start": v(19.85, -28.35) * mm, "mid": v(31.16, -23.66) * mm, "end": v(35.85, -12.35) * mm});
            skPoint(sketch, "E232.visualSharp", {"position": v(-35.85, -28.35) * mm});
            skArc(sketch, "E232.filletArc", {"start": v(-35.85, -12.35) * mm, "mid": v(-31.16, -23.66) * mm, "end": v(-19.85, -28.35) * mm});
            skSolve(sketch);
        }
        {
            var Q0;
            Q0 = qSketchRegion(id + "F34", true);
            extrude(context, id + "F35", {"entities" : qUnion([Q0]), "operationType" : NewBodyOperationType.REMOVE, "endBound" : BoundingType.THROUGH_ALL, "oppositeDirection" : true, "depth" : 25 * mm});
        }
        {
            var Q0;
            Q0=makeQuery(id+"F29.opExtrude","CAP_FACE",FACE,{"disambiguationData":[OSD([sQuery(id+"F28.wireOp",EDGE,"E182"),sQuery(id+"F28.wireOp",EDGE,"E183"),sQuery(id+"F28.wireOp",EDGE,"E184"),sQuery(id+"F28.wireOp",EDGE,"E190.MirrorCS"),sQuery(id+"F28.wireOp",EDGE,"E191.MirrorCS"),sQuery(id+"F28.wireOp",EDGE,"E192.MirrorCS"),sQuery(id+"F28.wireOp",EDGE,"E194.0"),sQuery(id+"F28.wireOp",EDGE,"E195.0"),sQuery(id+"F28.wireOp",EDGE,"E196.0"),sQuery(id+"F28.wireOp",EDGE,"E197.0"),sQuery(id+"F28.wireOp",EDGE,"E198.0"),sQuery(id+"F28.wireOp",EDGE,"E199.0"),sQuery(id+"F28.wireOp",EDGE,"E200.0"),sQuery(id+"F28.wireOp",EDGE,"E201.0"),sQuery(id+"F28.wireOp",EDGE,"E202.0"),sQuery(id+"F28.wireOp",EDGE,"E203.0"),sQuery(id+"F28.wireOp",EDGE,"E204.0"),sQuery(id+"F28.wireOp",EDGE,"E205.0"),sQuery(id+"F28.wireOp",EDGE,"E206.0"),sQuery(id+"F28.wireOp",EDGE,"E207.0"),sQuery(id+"F28.wireOp",EDGE,"E208.0"),sQuery(id+"F28.wireOp",EDGE,"E209.0"),sQuery(id+"F28.wireOp",EDGE,"E210"),sQuery(id+"F28.wireOp",EDGE,"E211"),sQuery(id+"F28.wireOp",EDGE,"E212"),sQuery(id+"F28.wireOp",EDGE,"E215"),sQuery(id+"F28.wireOp",EDGE,"E216"),sQuery(id+"F28.wireOp",EDGE,"E217"),sQuery(id+"F28.wireOp",EDGE,"E218.MirrorCS"),sQuery(id+"F28.wireOp",EDGE,"E219")])],"isStart":true});
            var sketch = newSketch(context, id + "F36", { "sketchPlane" : qUnion([Q0])});
            skLineSegment(sketch, "E233", {"start": v(0, 29.35) * mm, "end": v(0, 124.02) * mm, "construction": true});
            skLineSegment(sketch, "E234", {"start": v(-3.5, 121.02) * mm, "end": v(-6.5, 124.02) * mm});
            skArc(sketch, "E235", {"start": v(-3.5, 121.02) * mm, "mid": v(-3.6, 119.52) * mm, "end": v(-5.08, 119.82) * mm});
            skLineSegment(sketch, "E236", {"start": v(-5.08, 119.82) * mm, "end": v(-7.5, 119.82) * mm});
            skArc(sketch, "E237", {"start": v(-7.5, 119.82) * mm, "mid": v(-11.5, 115.82) * mm, "end": v(-7.5, 111.82) * mm});
            skLineSegment(sketch, "E238", {"start": v(-7.5, 111.82) * mm, "end": v(0, 111.82) * mm});
            skLineSegment(sketch, "E239", {"start": v(-6.5, 124.02) * mm, "end": v(0, 124.02) * mm});
            skLineSegment(sketch, "E240.MirrorCS", {"start": v(7.5, 111.82) * mm, "end": v(0, 111.82) * mm});
            skArc(sketch, "E241.MirrorCS", {"start": v(7.5, 119.82) * mm, "mid": v(11.5, 115.82) * mm, "end": v(7.5, 111.82) * mm});
            skLineSegment(sketch, "E242.MirrorCS", {"start": v(5.08, 119.82) * mm, "end": v(7.5, 119.82) * mm});
            skArc(sketch, "E243.MirrorCS", {"start": v(3.5, 121.02) * mm, "mid": v(3.6, 119.52) * mm, "end": v(5.08, 119.82) * mm});
            skLineSegment(sketch, "E244.MirrorCS", {"start": v(3.5, 121.02) * mm, "end": v(6.5, 124.02) * mm});
            skLineSegment(sketch, "E245.MirrorCS", {"start": v(6.5, 124.02) * mm, "end": v(0, 124.02) * mm});
            skLineSegment(sketch, "E246", {"start": v(-7.5, 115.82) * mm, "end": v(-17.86, 115.82) * mm, "construction": true});
            skPoint(sketch, "E246.endSnap0", {"position": v(-11.5, 115.82) * mm});
            skCircle(sketch, "E247", {"center": v(-17.86, 115.82) * mm, "radius": 2.7 * mm});
            skLineSegment(sketch, "E248.MirrorCS", {"start": v(7.5, 115.82) * mm, "end": v(17.86, 115.82) * mm, "construction": true});
            skCircle(sketch, "E249.MirrorC", {"center": v(17.86, 115.82) * mm, "radius": 2.7 * mm});
            skSolve(sketch);
        }
        {
            var Q0;
            Q0 = qSketchRegion(id + "F36", true);
            extrude(context, id + "F37", {"entities" : qUnion([Q0]), "operationType" : NewBodyOperationType.REMOVE, "endBound" : BoundingType.THROUGH_ALL, "oppositeDirection" : true, "depth" : 25 * mm});
        }
        {
            var Q0;
            Q0=makeQuery(id+"F29.opExtrude","CAP_FACE",FACE,{"disambiguationData":[OSD([sQuery(id+"F28.wireOp",EDGE,"E182"),sQuery(id+"F28.wireOp",EDGE,"E183"),sQuery(id+"F28.wireOp",EDGE,"E184"),sQuery(id+"F28.wireOp",EDGE,"E190.MirrorCS"),sQuery(id+"F28.wireOp",EDGE,"E191.MirrorCS"),sQuery(id+"F28.wireOp",EDGE,"E192.MirrorCS"),sQuery(id+"F28.wireOp",EDGE,"E194.0"),sQuery(id+"F28.wireOp",EDGE,"E195.0"),sQuery(id+"F28.wireOp",EDGE,"E196.0"),sQuery(id+"F28.wireOp",EDGE,"E197.0"),sQuery(id+"F28.wireOp",EDGE,"E198.0"),sQuery(id+"F28.wireOp",EDGE,"E199.0"),sQuery(id+"F28.wireOp",EDGE,"E200.0"),sQuery(id+"F28.wireOp",EDGE,"E201.0"),sQuery(id+"F28.wireOp",EDGE,"E202.0"),sQuery(id+"F28.wireOp",EDGE,"E203.0"),sQuery(id+"F28.wireOp",EDGE,"E204.0"),sQuery(id+"F28.wireOp",EDGE,"E205.0"),sQuery(id+"F28.wireOp",EDGE,"E206.0"),sQuery(id+"F28.wireOp",EDGE,"E207.0"),sQuery(id+"F28.wireOp",EDGE,"E208.0"),sQuery(id+"F28.wireOp",EDGE,"E209.0"),sQuery(id+"F28.wireOp",EDGE,"E210"),sQuery(id+"F28.wireOp",EDGE,"E211"),sQuery(id+"F28.wireOp",EDGE,"E212"),sQuery(id+"F28.wireOp",EDGE,"E215"),sQuery(id+"F28.wireOp",EDGE,"E216"),sQuery(id+"F28.wireOp",EDGE,"E217"),sQuery(id+"F28.wireOp",EDGE,"E218.MirrorCS"),sQuery(id+"F28.wireOp",EDGE,"E219")])],"isStart":true});
            var sketch = newSketch(context, id + "F38", { "sketchPlane" : qUnion([Q0])});
            skLineSegment(sketch, "E250", {"start": v(0, 0) * mm, "end": v(0, 71.97) * mm, "construction": true});
            skLineSegment(sketch, "E251", {"start": v(0, 71.97) * mm, "end": v(0, 81.97) * mm, "construction": true});
            skLineSegment(sketch, "E252", {"start": v(0, 81.97) * mm, "end": v(0, 111.82) * mm, "construction": true});
            skArc(sketch, "E253", {"start": v(-12.5, 81.97) * mm, "mid": v(0, 94.47) * mm, "end": v(12.5, 81.97) * mm});
            skArc(sketch, "E254", {"start": v(-12.5, 71.97) * mm, "mid": v(0, 59.47) * mm, "end": v(12.5, 71.97) * mm});
            skLineSegment(sketch, "E255", {"start": v(-12.5, 81.97) * mm, "end": v(-12.5, 71.97) * mm});
            skLineSegment(sketch, "E256", {"start": v(12.5, 81.97) * mm, "end": v(12.5, 71.97) * mm});
            skLineSegment(sketch, "E257", {"start": v(-23.57, 100.54) * mm, "end": v(0, 100.54) * mm, "construction": true});
            skLineSegment(sketch, "E258", {"start": v(0, 100.54) * mm, "end": v(23.57, 100.54) * mm, "construction": true});
            skLineSegment(sketch, "E259", {"start": v(23.57, 100.54) * mm, "end": v(0, 76.97) * mm, "construction": true});
            skLineSegment(sketch, "E260", {"start": v(0, 76.97) * mm, "end": v(-23.57, 53.4) * mm, "construction": true});
            skLineSegment(sketch, "E261", {"start": v(-23.57, 53.4) * mm, "end": v(0, 53.4) * mm, "construction": true});
            skLineSegment(sketch, "E262", {"start": v(0, 53.4) * mm, "end": v(23.57, 53.4) * mm, "construction": true});
            skLineSegment(sketch, "E263", {"start": v(23.57, 53.4) * mm, "end": v(0, 76.97) * mm, "construction": true});
            skLineSegment(sketch, "E264", {"start": v(0, 76.97) * mm, "end": v(-23.57, 100.54) * mm, "construction": true});
            skLineSegment(sketch, "E265", {"start": v(-23.57, 105.04) * mm, "end": v(-23.57, 96.04) * mm, "construction": true});
            skLineSegment(sketch, "E266", {"start": v(23.57, 105.04) * mm, "end": v(23.57, 96.04) * mm, "construction": true});
            skLineSegment(sketch, "E267", {"start": v(0, 76.97) * mm, "end": v(-12.5, 76.97) * mm, "construction": true});
            skLineSegment(sketch, "E268", {"start": v(-23.57, 57.9) * mm, "end": v(-23.57, 48.9) * mm, "construction": true});
            skLineSegment(sketch, "E269", {"start": v(23.57, 57.9) * mm, "end": v(23.57, 48.9) * mm, "construction": true});
            skArc(sketch, "E270", {"start": v(-26.07, 57.9) * mm, "mid": v(-23.57, 60.4) * mm, "end": v(-21.07, 57.9) * mm});
            skArc(sketch, "E271", {"start": v(-26.07, 48.9) * mm, "mid": v(-23.57, 46.4) * mm, "end": v(-21.07, 48.9) * mm});
            skLineSegment(sketch, "E272", {"start": v(-26.07, 57.9) * mm, "end": v(-26.07, 48.9) * mm});
            skLineSegment(sketch, "E273", {"start": v(-21.07, 57.9) * mm, "end": v(-21.07, 48.9) * mm});
            skArc(sketch, "E274.MirrorCS", {"start": v(26.07, 57.9) * mm, "mid": v(23.57, 60.4) * mm, "end": v(21.07, 57.9) * mm});
            skLineSegment(sketch, "E275.MirrorCS", {"start": v(26.07, 57.9) * mm, "end": v(26.07, 48.9) * mm});
            skLineSegment(sketch, "E276.MirrorCS", {"start": v(21.07, 57.9) * mm, "end": v(21.07, 48.9) * mm});
            skArc(sketch, "E277.MirrorCS", {"start": v(26.07, 48.9) * mm, "mid": v(23.57, 46.4) * mm, "end": v(21.07, 48.9) * mm});
            skLineSegment(sketch, "E278.MirrorCS", {"start": v(-26.07, 96.04) * mm, "end": v(-26.07, 105.04) * mm});
            skArc(sketch, "E279.MirrorCS", {"start": v(-26.07, 96.04) * mm, "mid": v(-23.57, 93.54) * mm, "end": v(-21.07, 96.04) * mm});
            skLineSegment(sketch, "E280.MirrorCS", {"start": v(-21.07, 96.04) * mm, "end": v(-21.07, 105.04) * mm});
            skArc(sketch, "E281.MirrorCS", {"start": v(-26.07, 105.04) * mm, "mid": v(-23.57, 107.54) * mm, "end": v(-21.07, 105.04) * mm});
            skArc(sketch, "E282.MirrorCS", {"start": v(26.07, 105.04) * mm, "mid": v(23.57, 107.54) * mm, "end": v(21.07, 105.04) * mm});
            skLineSegment(sketch, "E283.MirrorCS", {"start": v(21.07, 96.04) * mm, "end": v(21.07, 105.04) * mm});
            skArc(sketch, "E284.MirrorCS", {"start": v(26.07, 96.04) * mm, "mid": v(23.57, 93.54) * mm, "end": v(21.07, 96.04) * mm});
            skLineSegment(sketch, "E285.MirrorCS", {"start": v(26.07, 96.04) * mm, "end": v(26.07, 105.04) * mm});
            skSolve(sketch);
        }
        {
            var Q0;
            Q0 = qSketchRegion(id + "F38", true);
            extrude(context, id + "F39", {"entities" : qUnion([Q0]), "operationType" : NewBodyOperationType.REMOVE, "endBound" : BoundingType.THROUGH_ALL, "oppositeDirection" : true, "depth" : 25 * mm});
        }
    });
